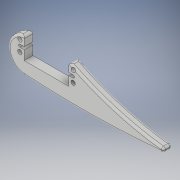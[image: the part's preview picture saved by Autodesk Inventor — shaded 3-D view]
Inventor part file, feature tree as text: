
AUTODESK INVENTOR PART (.ipt)
format: ipt  version: 2019 (Build 230136000, 136)  size: 201,216 bytes
history: native  units: mm
features: extrude x3, fillet x2, sketch x2, other x1
ambient origin geometry x8: Origin, YZ Plane, XZ Plane, XY Plane, X Axis, Y Axis, Z Axis, Center Point
bodies: Body1 (feature_tree)
feature tree (8):
  other  "Твердое тело1"
  extrude  "Выдавливание1"  Depth=143.0mm
  fillet  "Сопряжение1"  Radius=32.0mm
  fillet  "Сопряжение2"  Radius=15.0mm
  sketch  "Эскиз2"
  extrude  "Выдавливание2"  Depth=41.0mm
  extrude  "Выдавливание3"  Depth=6.0mm
  sketch  "Эскиз1"
